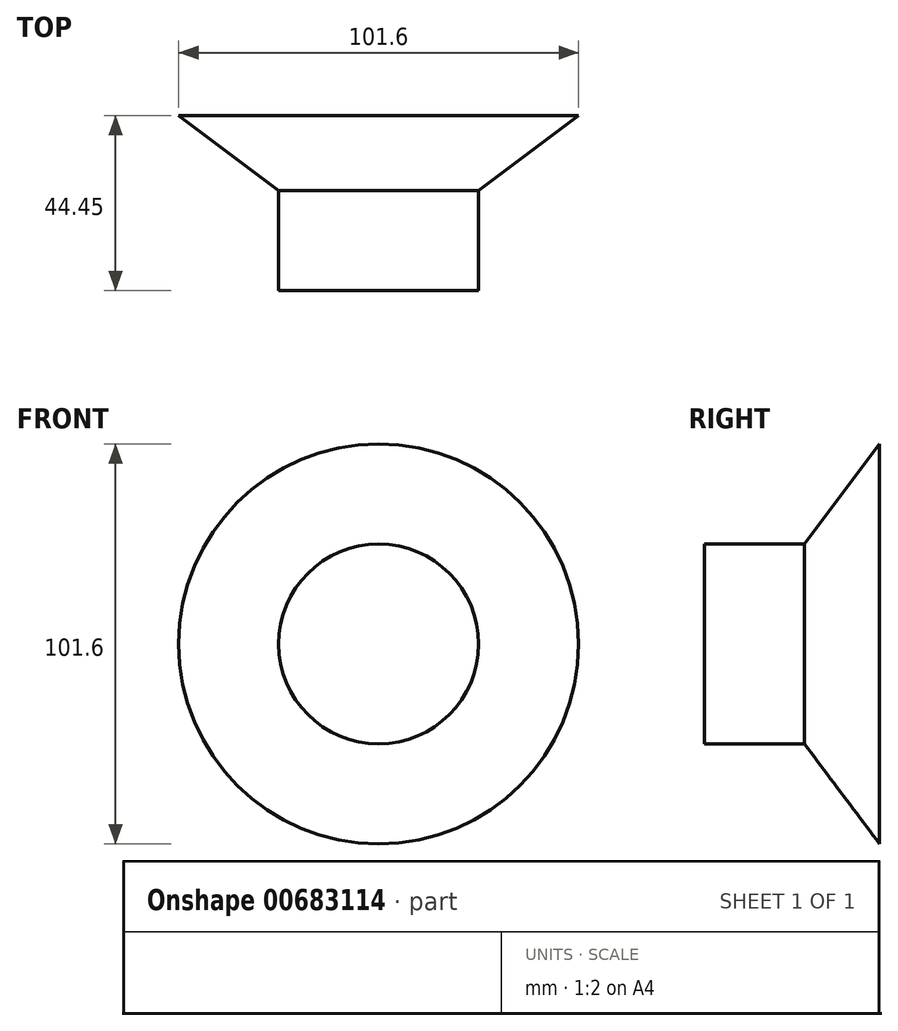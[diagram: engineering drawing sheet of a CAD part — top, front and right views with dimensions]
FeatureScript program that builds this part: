
annotation { "Feature Type Name" : "Feature", "Feature Type Description" : "" }
export const myFeature = defineFeature(function(context is Context, id is Id, definition is map)
    precondition{}
    {
        {
            var Q0;
            Q0=qCreatedBy(makeId("Front.planeOp"),FACE);
            var sketch = newSketch(context, id + "F0", { "sketchPlane" : qUnion([Q0])});
            skCircle(sketch, "E0", {"center": v(0, 0) * mm, "radius": 50.8 * mm});
            skSolve(sketch);
        }
        {
            var Q0;
            Q0=makeQuery(id+"F0.imprint","IMPRINT",FACE,{"disambiguationData":[TD([[makeQuery(id+"F0.imprint","IMPRINT",EDGE,{"derivedFrom":sQuery(id+"F0.wireOp",EDGE,"E0")}),1.0]])]});
            cPlane(context, id + "F1", {"entities" : qUnion([Q0]), "cplaneType" : CPlaneType.OFFSET, "offset" : 19.05 * mm, "width" : 152.4 * mm, "height" : 152.4 * mm});
        }
        {
            var Q0;
            Q0=qCreatedBy(id+"F1.planeOp",FACE);
            var sketch = newSketch(context, id + "F2", { "sketchPlane" : qUnion([Q0])});
            skCircle(sketch, "E1", {"center": v(0, 0) * mm, "radius": 25.4 * mm});
            skSolve(sketch);
        }
        {
            var Q0;
            Q0=makeQuery(id+"F0.imprint","IMPRINT",FACE,{"disambiguationData":[TD([[makeQuery(id+"F0.imprint","IMPRINT",EDGE,{"derivedFrom":sQuery(id+"F0.wireOp",EDGE,"E0")}),1.0]])]});
            var Q1;
            Q1=makeQuery(id+"F2.imprint","IMPRINT",FACE,{"disambiguationData":[TD([[makeQuery(id+"F2.imprint","IMPRINT",EDGE,{"derivedFrom":sQuery(id+"F2.wireOp",EDGE,"E1")}),1.0]])]});
            loft(context, id + "F3", {"sheetProfilesArray" : [{ "sheetProfileEntities" : qUnion([Q0]) }, { "sheetProfileEntities" : qUnion([Q1]) }]});
        }
        {
            var Q0;
            Q0=qSketchRegion(id+"F2",true);
            extrude(context, id + "F4", {"entities" : qUnion([Q0]), "operationType" : NewBodyOperationType.ADD, "depth" : 25.4 * mm, "offsetDistance" : 25.4 * mm});
        }
    });
